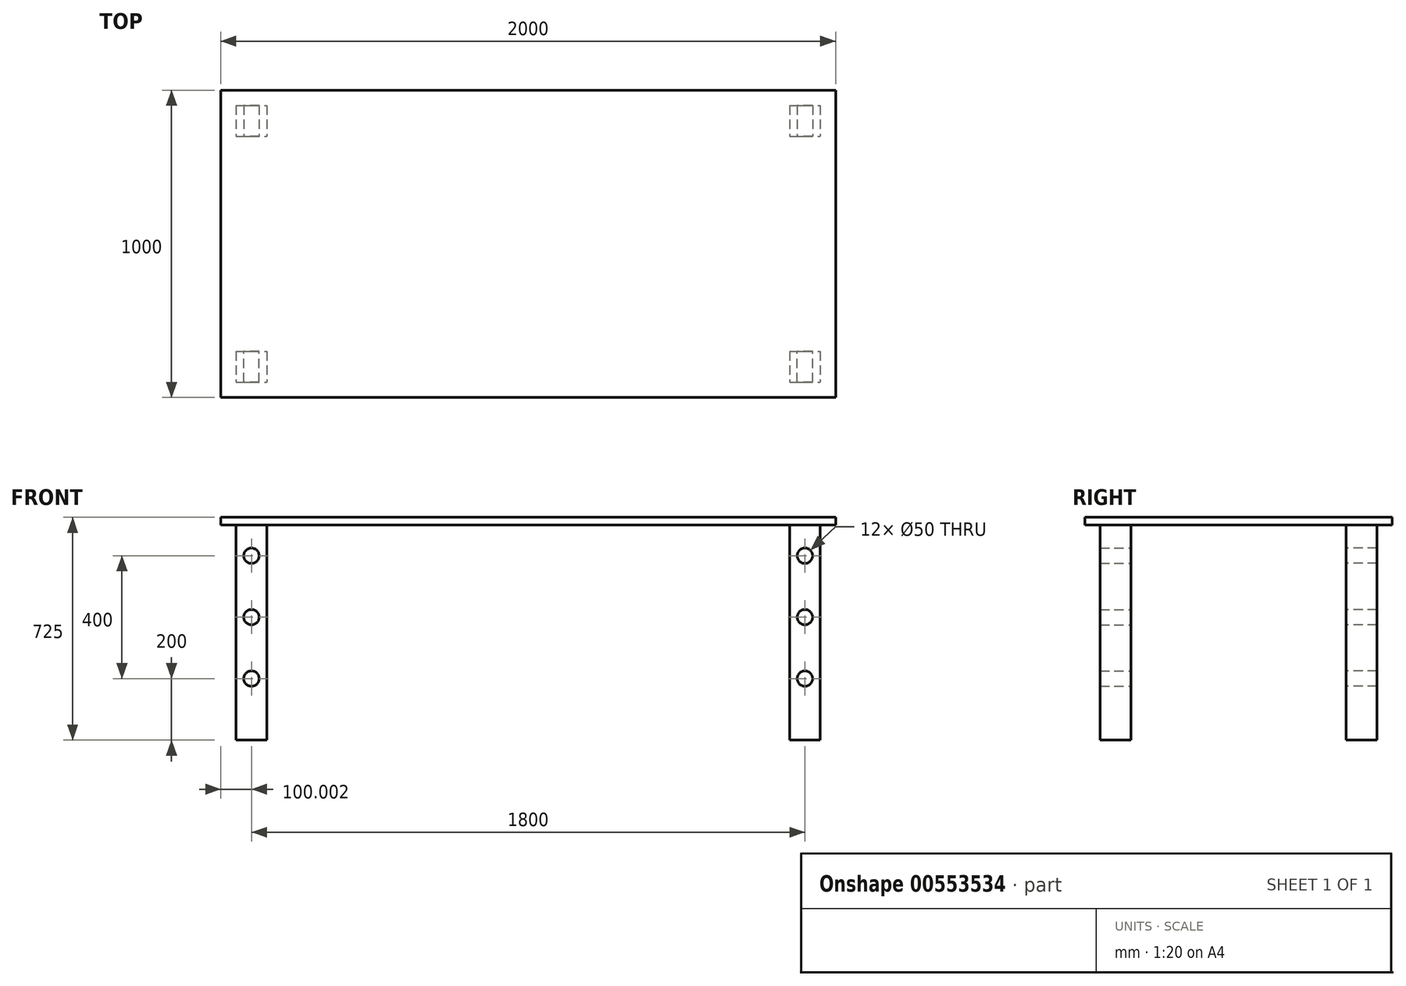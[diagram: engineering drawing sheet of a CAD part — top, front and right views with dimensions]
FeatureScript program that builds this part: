
annotation { "Feature Type Name" : "Feature", "Feature Type Description" : "" }
export const myFeature = defineFeature(function(context is Context, id is Id, definition is map)
    precondition{}
    {
        {
            var Q0;
            Q0=qCreatedBy(makeId("Top.planeOp"),FACE);
            var sketch = newSketch(context, id + "F0", { "sketchPlane" : qUnion([Q0])});
            skLineSegment(sketch, "E0.bottom", {"start": v(-1007.05, 533.18) * mm, "end": v(992.95, 533.18) * mm});
            skLineSegment(sketch, "E0.top", {"start": v(-1007.05, -466.82) * mm, "end": v(992.95, -466.82) * mm});
            skLineSegment(sketch, "E0.left", {"start": v(-1007.05, 533.18) * mm, "end": v(-1007.05, -466.82) * mm});
            skLineSegment(sketch, "E0.right", {"start": v(992.95, 533.18) * mm, "end": v(992.95, -466.82) * mm});
            skLineSegment(sketch, "E1.bottom", {"start": v(-957.05, 483.18) * mm, "end": v(-857.05, 483.18) * mm});
            skLineSegment(sketch, "E1.top", {"start": v(-957.05, 383.18) * mm, "end": v(-857.05, 383.18) * mm});
            skLineSegment(sketch, "E1.left", {"start": v(-957.05, 483.18) * mm, "end": v(-957.05, 383.18) * mm});
            skLineSegment(sketch, "E1.right", {"start": v(-857.05, 483.18) * mm, "end": v(-857.05, 383.18) * mm});
            skLineSegment(sketch, "E2.bottom", {"start": v(-957.05, -316.82) * mm, "end": v(-857.05, -316.82) * mm});
            skLineSegment(sketch, "E2.top", {"start": v(-957.05, -416.82) * mm, "end": v(-857.05, -416.82) * mm});
            skLineSegment(sketch, "E2.left", {"start": v(-957.05, -316.82) * mm, "end": v(-957.05, -416.82) * mm});
            skLineSegment(sketch, "E2.right", {"start": v(-857.05, -316.82) * mm, "end": v(-857.05, -416.82) * mm});
            skLineSegment(sketch, "E3.bottom", {"start": v(842.95, 483.18) * mm, "end": v(942.95, 483.18) * mm});
            skLineSegment(sketch, "E3.top", {"start": v(842.95, 383.18) * mm, "end": v(942.95, 383.18) * mm});
            skLineSegment(sketch, "E3.left", {"start": v(842.95, 483.18) * mm, "end": v(842.95, 383.18) * mm});
            skLineSegment(sketch, "E3.right", {"start": v(942.95, 483.18) * mm, "end": v(942.95, 383.18) * mm});
            skLineSegment(sketch, "E4.bottom", {"start": v(842.95, -316.82) * mm, "end": v(942.95, -316.82) * mm});
            skLineSegment(sketch, "E4.top", {"start": v(842.95, -416.82) * mm, "end": v(942.95, -416.82) * mm});
            skLineSegment(sketch, "E4.left", {"start": v(842.95, -316.82) * mm, "end": v(842.95, -416.82) * mm});
            skLineSegment(sketch, "E4.right", {"start": v(942.95, -316.82) * mm, "end": v(942.95, -416.82) * mm});
            skSolve(sketch);
        }
        {
            var Q0;
            Q0=qCreatedBy(makeId("Front.planeOp"),FACE);
            var sketch = newSketch(context, id + "F1", { "sketchPlane" : qUnion([Q0])});
            skCircle(sketch, "E5", {"center": v(-907.05, -500) * mm, "radius": 25 * mm});
            skCircle(sketch, "E6", {"center": v(-907.05, -300) * mm, "radius": 25 * mm});
            skCircle(sketch, "E7", {"center": v(-907.05, -100) * mm, "radius": 25 * mm});
            skCircle(sketch, "E8", {"center": v(892.95, -100) * mm, "radius": 25 * mm});
            skCircle(sketch, "E9", {"center": v(892.95, -300) * mm, "radius": 25 * mm});
            skCircle(sketch, "E10", {"center": v(892.95, -500) * mm, "radius": 25 * mm});
            skSolve(sketch);
        }
        {
            var Q0;
            Q0 = qSketchRegion(id + "F0", true);
            var Q1;
            Q1=makeQuery(id+"F0.imprint","IMPRINT",FACE,{"disambiguationData":[TD([[makeQuery(id+"F0.imprint","IMPRINT",EDGE,{"derivedFrom":sQuery(id+"F0.wireOp",EDGE,"E2.bottom")}),-1.0]])]});
            var Q2;
            Q2=makeQuery(id+"F0.imprint","IMPRINT",FACE,{"disambiguationData":[TD([[makeQuery(id+"F0.imprint","IMPRINT",EDGE,{"derivedFrom":sQuery(id+"F0.wireOp",EDGE,"E1.bottom")}),-1.0]])]});
            var Q3;
            Q3=makeQuery(id+"F0.imprint","IMPRINT",FACE,{"disambiguationData":[TD([[makeQuery(id+"F0.imprint","IMPRINT",EDGE,{"derivedFrom":sQuery(id+"F0.wireOp",EDGE,"E3.bottom")}),-1.0]])]});
            var Q4;
            Q4=makeQuery(id+"F0.imprint","IMPRINT",FACE,{"disambiguationData":[TD([[makeQuery(id+"F0.imprint","IMPRINT",EDGE,{"derivedFrom":sQuery(id+"F0.wireOp",EDGE,"E4.bottom")}),-1.0]])]});
            extrude(context, id + "F2", {"entities" : qUnion([Q0, Q1, Q2, Q3, Q4]), "depth" : 25 * mm, "offsetDistance" : 25 * mm});
        }
        {
            var Q0;
            Q0=makeQuery(id+"F0.imprint","IMPRINT",FACE,{"disambiguationData":[TD([[makeQuery(id+"F0.imprint","IMPRINT",EDGE,{"derivedFrom":sQuery(id+"F0.wireOp",EDGE,"E2.bottom")}),-1.0]])]});
            var Q1;
            Q1=makeQuery(id+"F0.imprint","IMPRINT",FACE,{"disambiguationData":[TD([[makeQuery(id+"F0.imprint","IMPRINT",EDGE,{"derivedFrom":sQuery(id+"F0.wireOp",EDGE,"E1.bottom")}),-1.0]])]});
            var Q2;
            Q2=makeQuery(id+"F0.imprint","IMPRINT",FACE,{"disambiguationData":[TD([[makeQuery(id+"F0.imprint","IMPRINT",EDGE,{"derivedFrom":sQuery(id+"F0.wireOp",EDGE,"E3.bottom")}),-1.0]])]});
            var Q3;
            Q3=makeQuery(id+"F0.imprint","IMPRINT",FACE,{"disambiguationData":[TD([[makeQuery(id+"F0.imprint","IMPRINT",EDGE,{"derivedFrom":sQuery(id+"F0.wireOp",EDGE,"E4.bottom")}),-1.0]])]});
            extrude(context, id + "F3", {"entities" : qUnion([Q0, Q1, Q2, Q3]), "operationType" : NewBodyOperationType.ADD, "oppositeDirection" : true, "depth" : 700 * mm, "offsetDistance" : 25 * mm});
        }
        {
            var Q0;
            Q0=sQuery(id+"F1.wireOp",VERTEX,"E7.center");
            var Q1;
            Q1=sQuery(id+"F1.wireOp",VERTEX,"E6.center");
            var Q2;
            Q2=sQuery(id+"F1.wireOp",VERTEX,"E5.center");
            var Q3;
            Q3=sQuery(id+"F1.wireOp",VERTEX,"E10.center");
            var Q4;
            Q4=sQuery(id+"F1.wireOp",VERTEX,"E9.center");
            var Q5;
            Q5=sQuery(id+"F1.wireOp",VERTEX,"E8.center");
            var Q6;
            Q6=makeQuery(id+"F2.opExtrude","SWEPT_BODY",BODY,{"disambiguationData":[OSD([sQuery(id+"F0.wireOp",EDGE,"E0.bottom"),sQuery(id+"F0.wireOp",EDGE,"E0.top"),sQuery(id+"F0.wireOp",EDGE,"E0.left"),sQuery(id+"F0.wireOp",EDGE,"E0.right")])]});
            hole(context, id + "F4", {"style" : HoleStyle.SIMPLE, "endStyle" : HoleEndStyle.THROUGH, "holeDiameter" : 50 * mm, "isTappedThrough" : true, "tappedDepth" : 12 * mm, "tapClearance" : 3, "locations" : qUnion([Q0, Q1, Q2, Q3, Q4, Q5]), "scope" : qUnion([Q6])});
        }
        {
            var Q0;
            Q0=sQuery(id+"F1.wireOp",VERTEX,"E7.center");
            var Q1;
            Q1=sQuery(id+"F1.wireOp",VERTEX,"E6.center");
            var Q2;
            Q2=sQuery(id+"F1.wireOp",VERTEX,"E5.center");
            var Q3;
            Q3=sQuery(id+"F1.wireOp",VERTEX,"E8.center");
            var Q4;
            Q4=sQuery(id+"F1.wireOp",VERTEX,"E9.center");
            var Q5;
            Q5=sQuery(id+"F1.wireOp",VERTEX,"E10.center");
            var Q6;
            Q6=makeQuery(id+"F2.opExtrude","SWEPT_BODY",BODY,{"disambiguationData":[OSD([sQuery(id+"F0.wireOp",EDGE,"E0.bottom"),sQuery(id+"F0.wireOp",EDGE,"E0.top"),sQuery(id+"F0.wireOp",EDGE,"E0.left"),sQuery(id+"F0.wireOp",EDGE,"E0.right")])]});
            hole(context, id + "F5", {"style" : HoleStyle.SIMPLE, "endStyle" : HoleEndStyle.THROUGH, "oppositeDirection" : true, "holeDiameter" : 50 * mm, "isTappedThrough" : true, "tappedDepth" : 12 * mm, "tapClearance" : 3, "locations" : qUnion([Q0, Q1, Q2, Q3, Q4, Q5]), "scope" : qUnion([Q6])});
        }
    });
